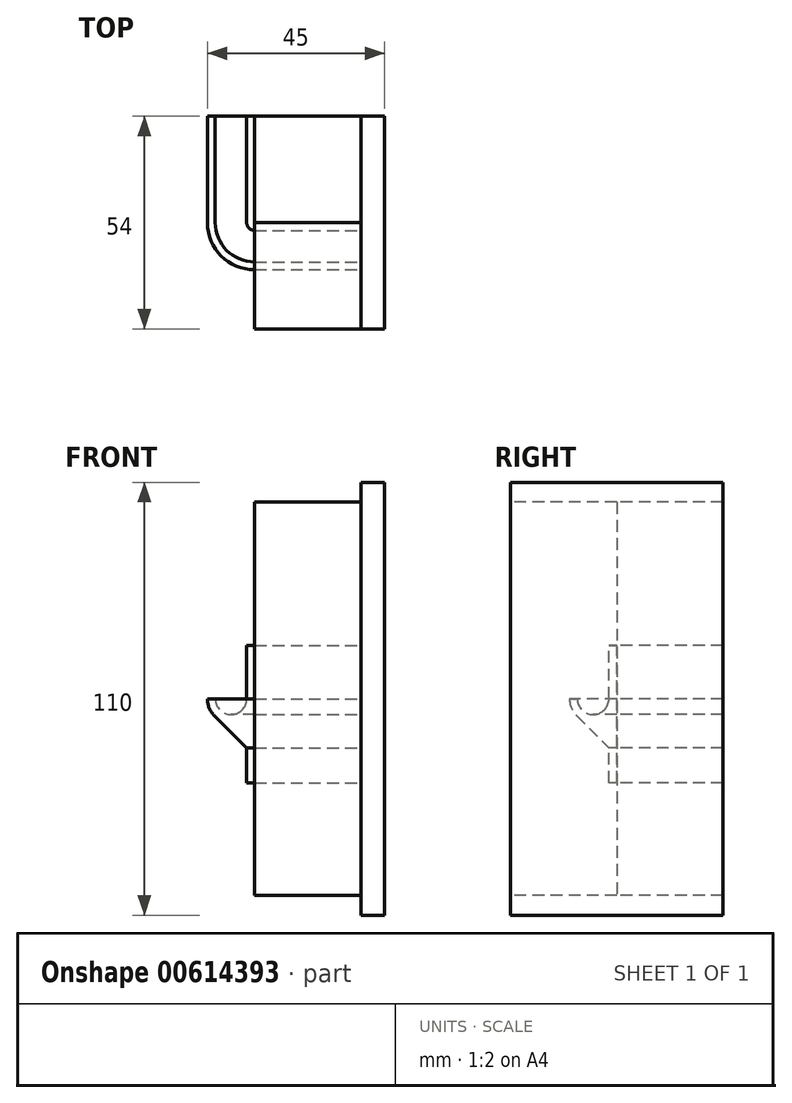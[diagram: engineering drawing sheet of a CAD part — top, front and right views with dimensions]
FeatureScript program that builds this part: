
annotation { "Feature Type Name" : "Feature", "Feature Type Description" : "" }
export const myFeature = defineFeature(function(context is Context, id is Id, definition is map)
    precondition{}
    {
        {
            var Q0;
            Q0=qCreatedBy(makeId("Top.planeOp"),FACE);
            var sketch = newSketch(context, id + "F0", { "sketchPlane" : qUnion([Q0])});
            skLineSegment(sketch, "E0.bottom", {"start": v(-13.5, 0) * mm, "end": v(13.5, 0) * mm});
            skLineSegment(sketch, "E0.top", {"start": v(-13.5, -27) * mm, "end": v(13.5, -27) * mm});
            skLineSegment(sketch, "E0.left", {"start": v(-13.5, 0) * mm, "end": v(-13.5, -27) * mm});
            skLineSegment(sketch, "E0.right", {"start": v(13.5, 0) * mm, "end": v(13.5, -27) * mm});
            skLineSegment(sketch, "E1.bottom", {"start": v(13.5, 0) * mm, "end": v(19.5, 0) * mm});
            skLineSegment(sketch, "E1.top", {"start": v(13.5, -54) * mm, "end": v(19.5, -54) * mm});
            skLineSegment(sketch, "E1.left", {"start": v(13.5, 0) * mm, "end": v(13.5, -54) * mm});
            skLineSegment(sketch, "E1.right", {"start": v(19.5, 0) * mm, "end": v(19.5, -54) * mm});
            skSolve(sketch);
        }
        {
            var Q0;
            {var subQ0=sQuery(id+"F0.wireOp",EDGE,"E0.bottom");Q0=makeQuery(id+"F0.imprint","IMPRINT",FACE,{"disambiguationData":[TD([[makeQuery(id+"F0.imprint","IMPRINT",EDGE,{"derivedFrom":subQ0}),-1.0]])]});}
            extrude(context, id + "F1", {"entities" : qUnion([Q0]), "depth" : 50 * mm, "offsetDistance" : 25 * mm, "hasSecondDirection" : true, "secondDirectionOppositeDirection" : true, "secondDirectionDepth" : 50 * mm});
        }
        {
            var Q0;
            Q0=makeQuery(id+"F1.opExtrude","SWEPT_BODY",BODY,{"disambiguationData":[OSD([sQuery(id+"F0.wireOp",EDGE,"E0.bottom"),sQuery(id+"F0.wireOp",EDGE,"E0.top"),sQuery(id+"F0.wireOp",EDGE,"E0.left"),sQuery(id+"F0.wireOp",EDGE,"E0.right")])]});
            var Q1;
            Q1=makeQuery(id+"F1.opExtrude","CAP_EDGE",EDGE,{"disambiguationData":[OSD([sQuery(id+"F0.wireOp",EDGE,"E0.left")])],"isStart":false});
            transform(context, id + "F2", {"entities" : qUnion([Q0]), "transformType" : TransformType.TRANSLATION_ENTITY, "oppositeDirectionEntity" : false, "transformLine" : qUnion([Q1]), "makeCopy" : true});
        }
        {
            var Q0;
            {var subQ3=sQuery(id+"F0.wireOp",EDGE,"E1.bottom");Q0=makeQuery(id+"F0.imprint","IMPRINT",FACE,{"disambiguationData":[TD([[makeQuery(id+"F0.imprint","IMPRINT",EDGE,{"derivedFrom":subQ3}),-1.0]])]});}
            extrude(context, id + "F3", {"entities" : qUnion([Q0]), "depth" : 55 * mm, "offsetDistance" : 25 * mm, "hasSecondDirection" : true, "secondDirectionOppositeDirection" : true, "secondDirectionDepth" : 55 * mm});
        }
        {
            var Q0;
            Q0=qCreatedBy(makeId("Top.planeOp"),FACE);
            var sketch = newSketch(context, id + "F4", { "sketchPlane" : qUnion([Q0])});
            skLineSegment(sketch, "E2", {"start": v(-13.5, 0) * mm, "end": v(-13.5, -27) * mm});
            skLineSegment(sketch, "E3", {"start": v(-13.5, -27) * mm, "end": v(13.5, -27) * mm});
            skLineSegment(sketch, "E4.0", {"start": v(-13.5, -32) * mm, "end": v(13.5, -32) * mm});
            skLineSegment(sketch, "E4.1", {"start": v(-18.5, 0) * mm, "end": v(-18.5, -27) * mm});
            skPoint(sketch, "E5.visualSharp", {"position": v(-18.5, -32) * mm});
            skArc(sketch, "E5.filletArc", {"start": v(-18.5, -27) * mm, "mid": v(-17.04, -30.54) * mm, "end": v(-13.5, -32) * mm});
            skSolve(sketch);
        }
        {
            var Q0;
            Q0=qCreatedBy(makeId("Front.planeOp"),FACE);
            var sketch = newSketch(context, id + "F5", { "sketchPlane" : qUnion([Q0])});
            skCircle(sketch, "E6", {"center": v(-19.5, 0) * mm, "radius": 6 * mm, "construction": true});
            skArc(sketch, "E7", {"start": v(-13.5, 0) * mm, "mid": v(-19.5, -6) * mm, "end": v(-25.5, 0) * mm});
            skArc(sketch, "E8", {"start": v(-15.5, 0) * mm, "mid": v(-19.5, -4) * mm, "end": v(-23.5, 0) * mm});
            skLineSegment(sketch, "E9", {"start": v(-25.5, 0) * mm, "end": v(-23.5, 0) * mm});
            skLineSegment(sketch, "E10", {"start": v(-15.5, 0) * mm, "end": v(-13.5, 0) * mm});
            skLineSegment(sketch, "E11", {"start": v(-19.5, 0) * mm, "end": v(-19.5, -6) * mm, "construction": true});
            skLineSegment(sketch, "E12", {"start": v(-23.74, -4.24) * mm, "end": v(-13.5, -14.49) * mm});
            skLineSegment(sketch, "E13", {"start": v(-13.5, -14.49) * mm, "end": v(-13.5, 0) * mm});
            skLineSegment(sketch, "E14", {"start": v(-13.5, -14.49) * mm, "end": v(-13.5, -21.34) * mm});
            skLineSegment(sketch, "E15", {"start": v(-13.5, -21.34) * mm, "end": v(-15.5, -21.34) * mm});
            skLineSegment(sketch, "E16", {"start": v(-15.5, -21.34) * mm, "end": v(-15.5, -12.49) * mm});
            skLineSegment(sketch, "E17", {"start": v(-15.5, 0) * mm, "end": v(-15.5, 13.59) * mm});
            skLineSegment(sketch, "E18", {"start": v(-15.5, 13.59) * mm, "end": v(-13.5, 13.59) * mm});
            skLineSegment(sketch, "E19", {"start": v(-13.5, 13.59) * mm, "end": v(-13.5, 0) * mm});
            skSolve(sketch);
        }
        {
            var Q0;
            Q0=makeQuery(id+"F5.imprint","IMPRINT",FACE,{"disambiguationData":[TD([[makeQuery(id+"F5.imprint","IMPRINT",EDGE,{"derivedFrom":sQuery(id+"F5.wireOp",EDGE,"E7")}),-1.0]])]});
            var Q1;
            {var subQ2=sQuery(id+"F5.wireOp",EDGE,"E12");Q1=makeQuery(id+"F5.imprint","IMPRINT",FACE,{"disambiguationData":[TD([[makeQuery(id+"F5.imprint","IMPRINT",EDGE,{"derivedFrom":subQ2}),1.0]])]});}
            var Q2;
            {var subQ0=sQuery(id+"F5.wireOp",EDGE,"E10");Q2=makeQuery(id+"F5.imprint","IMPRINT",FACE,{"disambiguationData":[TD([[makeQuery(id+"F5.imprint","IMPRINT",EDGE,{"derivedFrom":subQ0}),-1.0]])]});}
            var Q3;
            Q3=makeQuery(id+"F5.imprint","IMPRINT",FACE,{"disambiguationData":[TD([[makeQuery(id+"F5.imprint","IMPRINT",EDGE,{"derivedFrom":sQuery(id+"F5.wireOp",EDGE,"E10")}),1.0]])]});
            var Q4;
            {var subQ0=sQuery(id+"F5.wireOp",EDGE,"E14");Q4=makeQuery(id+"F5.imprint","IMPRINT",FACE,{"disambiguationData":[TD([[makeQuery(id+"F5.imprint","IMPRINT",EDGE,{"derivedFrom":subQ0}),-1.0]])]});}
            var Q5;
            Q5=sQuery(id+"F4.wireOp",EDGE,"E4.1");
            var Q6;
            Q6=sQuery(id+"F4.wireOp",EDGE,"E5.filletArc");
            var Q7;
            Q7=sQuery(id+"F4.wireOp",EDGE,"E4.0");
            sweep(context, id + "F6", {"profiles" : qUnion([Q0, Q1, Q2, Q3, Q4]), "path" : qUnion([Q5, Q6, Q7])});
        }
    });
